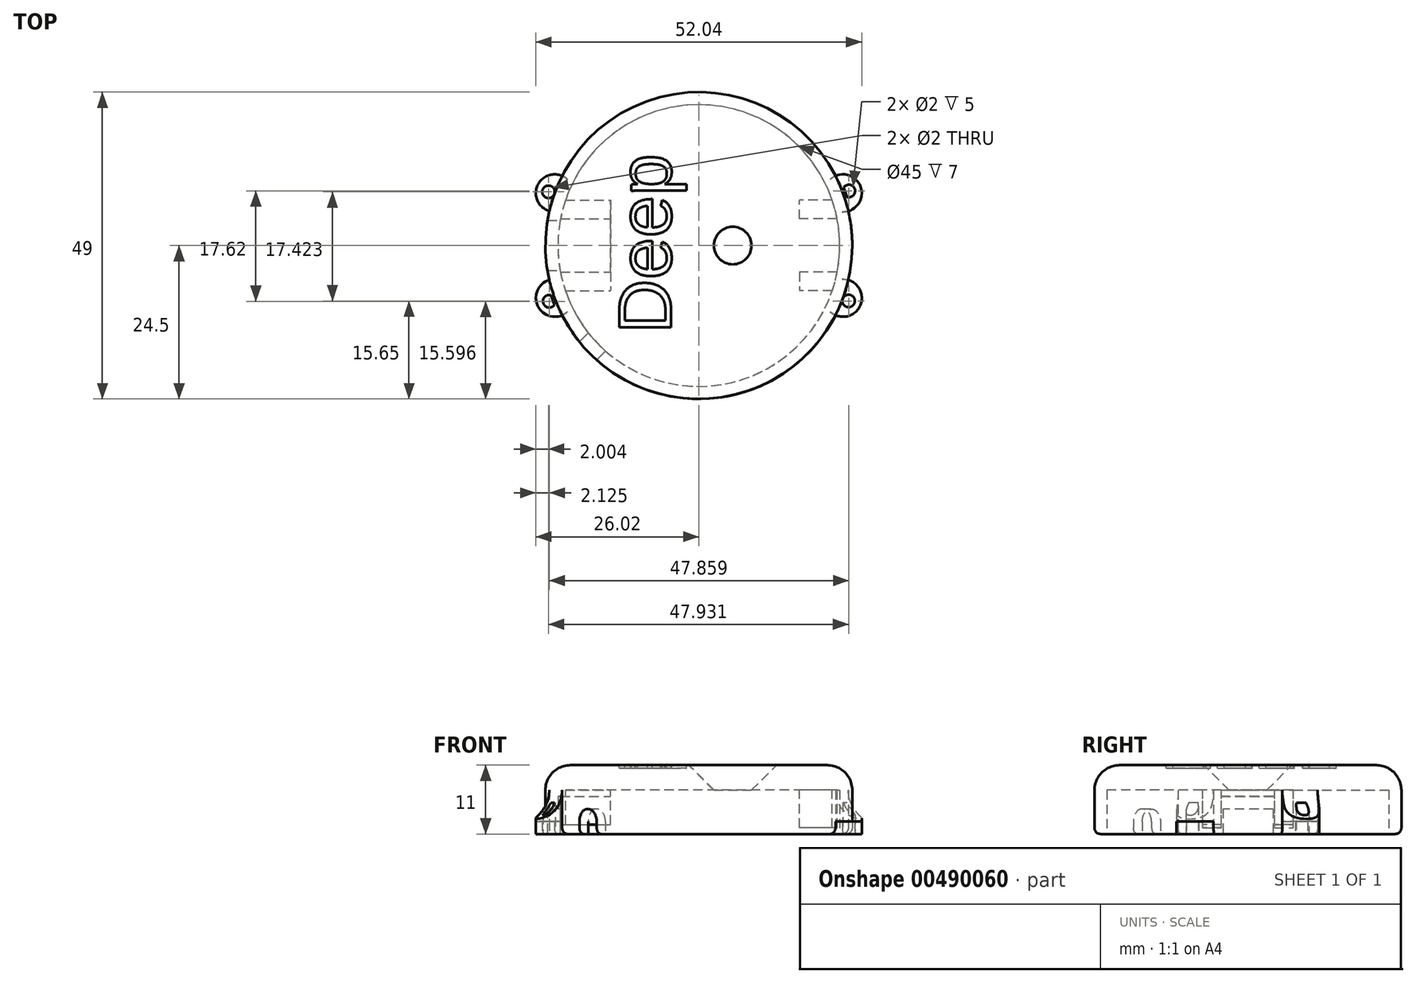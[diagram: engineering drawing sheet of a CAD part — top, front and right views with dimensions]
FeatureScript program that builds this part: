
annotation { "Feature Type Name" : "Feature", "Feature Type Description" : "" }
export const myFeature = defineFeature(function(context is Context, id is Id, definition is map)
    precondition{}
    {
        {
            var Q0;
            Q0=qCreatedBy(makeId("Top.planeOp"),FACE);
            var sketch = newSketch(context, id + "F0", { "sketchPlane" : qUnion([Q0])});
            skCircle(sketch, "E0", {"center": v(0, 0) * mm, "radius": 24.5 * mm});
            skSolve(sketch);
        }
        {
            var Q0;
            Q0=makeQuery(id+"F0.imprint","IMPRINT",FACE,{"disambiguationData":[TD([[makeQuery(id+"F0.imprint","IMPRINT",EDGE,{"derivedFrom":sQuery(id+"F0.wireOp",EDGE,"E0")}),1.0]])]});
            extrude(context, id + "F1", {"entities" : qUnion([Q0]), "depth" : 9 * mm});
        }
        {
            var Q0;
            Q0=makeQuery(id+"F1.opExtrude","CAP_FACE",FACE,{"disambiguationData":[OSD([sQuery(id+"F0.wireOp",EDGE,"E0")])],"isStart":true});
            shell(context, id + "F2", {"entities" : qUnion([Q0]), "thickness" : 2 * mm});
        }
        {
            var Q0;
            Q0=makeQuery(id+"F1.opExtrude","CAP_FACE",FACE,{"disambiguationData":[OSD([sQuery(id+"F0.wireOp",EDGE,"E0")])],"isStart":true});
            var sketch = newSketch(context, id + "F3", { "sketchPlane" : qUnion([Q0])});
            skLineSegment(sketch, "E1.bottom", {"start": v(-26.55, 4) * mm, "end": v(-19.55, 4) * mm});
            skLineSegment(sketch, "E1.top", {"start": v(-26.55, -4) * mm, "end": v(-19.55, -4) * mm});
            skLineSegment(sketch, "E1.left", {"start": v(-26.55, 4) * mm, "end": v(-26.55, -4) * mm});
            skLineSegment(sketch, "E1.right", {"start": v(-19.55, 4) * mm, "end": v(-19.55, -4) * mm});
            skSolve(sketch);
        }
        {
            var Q0;
            {var subQ0=sQuery(id+"F3.wireOp",EDGE,"E1.bottom");var subQ1=sQuery(id+"F0.wireOp",EDGE,"E0");var subQ2=makeQuery(id+"F1.opExtrude","CAP_EDGE",EDGE,{"disambiguationData":[OSD([subQ1])],"isStart":true});var subQ3=makeQuery(id+"F3.imprint","INTERSECT",VERTEX,{"derivedFrom":[subQ2,subQ0]});Q0=makeQuery(id+"F3.imprint","IMPRINT",FACE,{"disambiguationData":[TD([[makeQuery(id+"F3.imprint","IMPRINT",EDGE,{"disambiguationData":[TD([[subQ3,1.0]])],"derivedFrom":subQ2}),-1.0]])]});}
            extrude(context, id + "F4", {"entities" : qUnion([Q0]), "operationType" : NewBodyOperationType.REMOVE, "oppositeDirection" : true, "depth" : 5 * mm});
        }
        {
            var Q0;
            {var subQ0=sQuery(id+"F0.wireOp",EDGE,"E0");Q0=makeQuery(id+"F2.opShell","OFFSET_FACE",FACE,{"disambiguationData":[OSD([subQ0]),TDD([makeQuery(id+"F1.opExtrude","CAP_FACE",FACE,{"disambiguationData":[OSD([subQ0])],"isStart":false})])]});}
            var sketch = newSketch(context, id + "F5", { "sketchPlane" : qUnion([Q0])});
            skLineSegment(sketch, "E2.bottom", {"start": v(-22.1, 4.25) * mm, "end": v(-14.1, 4.25) * mm});
            skLineSegment(sketch, "E2.top", {"start": v(-22.1, 7.25) * mm, "end": v(-14.1, 7.25) * mm});
            skLineSegment(sketch, "E2.left", {"start": v(-22.1, 4.25) * mm, "end": v(-22.1, 7.25) * mm});
            skLineSegment(sketch, "E2.right", {"start": v(-14.1, 4.25) * mm, "end": v(-14.1, 7.25) * mm});
            skLineSegment(sketch, "E3.bottom", {"start": v(-22.1, -4.25) * mm, "end": v(-14.1, -4.25) * mm});
            skLineSegment(sketch, "E3.top", {"start": v(-22.1, -7.25) * mm, "end": v(-14.1, -7.25) * mm});
            skLineSegment(sketch, "E3.left", {"start": v(-22.1, -4.25) * mm, "end": v(-22.1, -7.25) * mm});
            skLineSegment(sketch, "E3.right", {"start": v(-14.1, -4.25) * mm, "end": v(-14.1, -7.25) * mm});
            skLineSegment(sketch, "E4.bottom", {"start": v(22.1, 4.25) * mm, "end": v(16.1, 4.25) * mm});
            skLineSegment(sketch, "E4.top", {"start": v(22.1, 7.25) * mm, "end": v(16.1, 7.25) * mm});
            skLineSegment(sketch, "E4.left", {"start": v(22.1, 4.25) * mm, "end": v(22.1, 7.25) * mm});
            skLineSegment(sketch, "E4.right", {"start": v(16.1, 4.25) * mm, "end": v(16.1, 7.25) * mm});
            skLineSegment(sketch, "E5.bottom", {"start": v(22.1, -4.25) * mm, "end": v(16.1, -4.25) * mm});
            skLineSegment(sketch, "E5.top", {"start": v(22.1, -7.25) * mm, "end": v(16.1, -7.25) * mm});
            skLineSegment(sketch, "E5.left", {"start": v(22.1, -4.25) * mm, "end": v(22.1, -7.25) * mm});
            skLineSegment(sketch, "E5.right", {"start": v(16.1, -4.25) * mm, "end": v(16.1, -7.25) * mm});
            skSolve(sketch);
        }
        {
            var Q0;
            {var subQ0=sQuery(id+"F5.wireOp",EDGE,"E2.bottom");Q0=makeQuery(id+"F5.imprint","IMPRINT",FACE,{"disambiguationData":[TD([[makeQuery(id+"F5.imprint","IMPRINT",EDGE,{"derivedFrom":subQ0}),1.0]])]});}
            var Q1;
            {var subQ0=sQuery(id+"F5.wireOp",EDGE,"E3.bottom");Q1=makeQuery(id+"F5.imprint","IMPRINT",FACE,{"disambiguationData":[TD([[makeQuery(id+"F5.imprint","IMPRINT",EDGE,{"derivedFrom":subQ0}),-1.0]])]});}
            var Q2;
            {var subQ0=sQuery(id+"F5.wireOp",EDGE,"E4.bottom");Q2=makeQuery(id+"F5.imprint","IMPRINT",FACE,{"disambiguationData":[TD([[makeQuery(id+"F5.imprint","IMPRINT",EDGE,{"derivedFrom":subQ0}),-1.0]])]});}
            var Q3;
            {var subQ0=sQuery(id+"F5.wireOp",EDGE,"E5.bottom");Q3=makeQuery(id+"F5.imprint","IMPRINT",FACE,{"disambiguationData":[TD([[makeQuery(id+"F5.imprint","IMPRINT",EDGE,{"derivedFrom":subQ0}),1.0]])]});}
            extrude(context, id + "F6", {"entities" : qUnion([Q0, Q1, Q2, Q3]), "operationType" : NewBodyOperationType.ADD, "depth" : 6 * mm});
        }
        {
            var Q0;
            Q0=makeQuery(id+"F1.opExtrude","CAP_FACE",FACE,{"disambiguationData":[OSD([sQuery(id+"F0.wireOp",EDGE,"E0")])],"isStart":true});
            var sketch = newSketch(context, id + "F7", { "sketchPlane" : qUnion([Q0])});
            skLineSegment(sketch, "E6", {"start": v(0, 0) * mm, "end": v(60.5, -22.02) * mm, "construction": true});
            skLineSegment(sketch, "E7", {"start": v(0, 0) * mm, "end": v(-61.16, 22.26) * mm, "construction": true});
            skLineSegment(sketch, "E8", {"start": v(0, 0) * mm, "end": v(57.48, 20.92) * mm, "construction": true});
            skLineSegment(sketch, "E9", {"start": v(0, 0) * mm, "end": v(-59.66, -21.71) * mm, "construction": true});
            skArc(sketch, "E10", {"start": v(-21.83, 11.13) * mm, "mid": v(-25.84, 9.4) * mm, "end": v(-23.87, 5.5) * mm});
            skPoint(sketch, "E10.startSnap0", {"position": v(-30.58, 11.13) * mm});
            skArc(sketch, "E11", {"start": v(-23.87, -5.5) * mm, "mid": v(-25.84, -9.4) * mm, "end": v(-21.83, -11.13) * mm});
            skArc(sketch, "E12", {"start": v(21.83, -11.13) * mm, "mid": v(25.84, -9.4) * mm, "end": v(23.87, -5.5) * mm});
            skArc(sketch, "E13", {"start": v(23.87, 5.5) * mm, "mid": v(25.84, 9.4) * mm, "end": v(21.83, 11.13) * mm});
            skSolve(sketch);
        }
        {
            var Q0;
            {var subQ0=sQuery(id+"F7.wireOp",EDGE,"E10");Q0=makeQuery(id+"F7.imprint","IMPRINT",FACE,{"disambiguationData":[TD([[makeQuery(id+"F7.imprint","IMPRINT",EDGE,{"derivedFrom":subQ0}),1.0]])]});}
            var Q1;
            {var subQ0=sQuery(id+"F7.wireOp",EDGE,"E13");Q1=makeQuery(id+"F7.imprint","IMPRINT",FACE,{"disambiguationData":[TD([[makeQuery(id+"F7.imprint","IMPRINT",EDGE,{"derivedFrom":subQ0}),1.0]])]});}
            var Q2;
            {var subQ0=sQuery(id+"F7.wireOp",EDGE,"E12");Q2=makeQuery(id+"F7.imprint","IMPRINT",FACE,{"disambiguationData":[TD([[makeQuery(id+"F7.imprint","IMPRINT",EDGE,{"derivedFrom":subQ0}),1.0]])]});}
            var Q3;
            {var subQ0=sQuery(id+"F7.wireOp",EDGE,"E11");Q3=makeQuery(id+"F7.imprint","IMPRINT",FACE,{"disambiguationData":[TD([[makeQuery(id+"F7.imprint","IMPRINT",EDGE,{"derivedFrom":subQ0}),1.0]])]});}
            var Q4;
            Q4=makeQuery(id+"F1.opExtrude","CAP_FACE",FACE,{"disambiguationData":[OSD([sQuery(id+"F0.wireOp",EDGE,"E0")])],"isStart":false});
            extrude(context, id + "F8", {"entities" : qUnion([Q0, Q1, Q2, Q3, Q4]), "operationType" : NewBodyOperationType.ADD, "oppositeDirection" : true, "depth" : 2 * mm});
        }
        {
            var Q0;
            {var subQ0=sQuery(id+"F7.wireOp",EDGE,"E11");var subQ1=sQuery(id+"F0.wireOp",EDGE,"E0");var subQ2=makeQuery(id+"F1.opExtrude","CAP_EDGE",EDGE,{"disambiguationData":[OSD([subQ1])],"isStart":true});Q0=makeQuery(id+"F8.opExtrude","CAP_EDGE",EDGE,{"disambiguationData":[OSD([subQ1]),TDD([makeQuery(id+"F7.imprint","IMPRINT",EDGE,{"disambiguationData":[TD([[makeQuery(id+"F7.imprint","INTERSECT",VERTEX,{"disambiguationData":[OD(0.0)],"derivedFrom":[subQ2,subQ0]}),1.0]])],"derivedFrom":subQ2})])],"isStart":false});}
            var Q1;
            {var subQ0=sQuery(id+"F7.wireOp",EDGE,"E10");var subQ1=sQuery(id+"F0.wireOp",EDGE,"E0");var subQ2=makeQuery(id+"F1.opExtrude","CAP_EDGE",EDGE,{"disambiguationData":[OSD([subQ1])],"isStart":true});Q1=makeQuery(id+"F8.opExtrude","CAP_EDGE",EDGE,{"disambiguationData":[OSD([subQ1]),TDD([makeQuery(id+"F7.imprint","IMPRINT",EDGE,{"disambiguationData":[TD([[makeQuery(id+"F7.imprint","INTERSECT",VERTEX,{"disambiguationData":[OD(0.0)],"derivedFrom":[subQ2,subQ0]}),1.0]])],"derivedFrom":subQ2})])],"isStart":false});}
            var Q2;
            {var subQ0=sQuery(id+"F7.wireOp",EDGE,"E12");var subQ1=sQuery(id+"F0.wireOp",EDGE,"E0");var subQ2=makeQuery(id+"F1.opExtrude","CAP_EDGE",EDGE,{"disambiguationData":[OSD([subQ1])],"isStart":true});Q2=makeQuery(id+"F8.opExtrude","CAP_EDGE",EDGE,{"disambiguationData":[OSD([subQ1]),TDD([makeQuery(id+"F7.imprint","IMPRINT",EDGE,{"disambiguationData":[TD([[makeQuery(id+"F7.imprint","INTERSECT",VERTEX,{"disambiguationData":[OD(0.0)],"derivedFrom":[subQ2,subQ0]}),1.0]])],"derivedFrom":subQ2})])],"isStart":false});}
            var Q3;
            {var subQ0=sQuery(id+"F7.wireOp",EDGE,"E13");var subQ1=sQuery(id+"F0.wireOp",EDGE,"E0");var subQ2=makeQuery(id+"F1.opExtrude","CAP_EDGE",EDGE,{"disambiguationData":[OSD([subQ1])],"isStart":true});Q3=makeQuery(id+"F8.opExtrude","CAP_EDGE",EDGE,{"disambiguationData":[OSD([subQ1]),TDD([makeQuery(id+"F7.imprint","IMPRINT",EDGE,{"disambiguationData":[TD([[makeQuery(id+"F7.imprint","INTERSECT",VERTEX,{"disambiguationData":[OD(0.0)],"derivedFrom":[subQ2,subQ0]}),1.0]])],"derivedFrom":subQ2})])],"isStart":false});}
            fillet(context, id + "F9", {"entities" : qUnion([Q0, Q1, Q2, Q3]), "radius" : 5 * mm, "tangentPropagation" : true, "allowEdgeOverflow" : false});
        }
        {
            var Q0;
            {var subQ0=sQuery(id+"F0.wireOp",EDGE,"E0");Q0=makeQuery(id+"F8.boolean.opBoolean","MERGE",FACE,{"derivedFrom":[makeQuery(id+"F1.opExtrude","CAP_FACE",FACE,{"disambiguationData":[OSD([subQ0])],"isStart":true}),makeQuery(id+"F8.opExtrude","CAP_FACE",FACE,{"disambiguationData":[OSD([subQ0,sQuery(id+"F7.wireOp",EDGE,"E10")])],"isStart":true}),makeQuery(id+"F8.opExtrude","CAP_FACE",FACE,{"disambiguationData":[OSD([subQ0,sQuery(id+"F7.wireOp",EDGE,"E11")])],"isStart":true}),makeQuery(id+"F8.opExtrude","CAP_FACE",FACE,{"disambiguationData":[OSD([subQ0,sQuery(id+"F7.wireOp",EDGE,"E12")])],"isStart":true}),makeQuery(id+"F8.opExtrude","CAP_FACE",FACE,{"disambiguationData":[OSD([subQ0,sQuery(id+"F7.wireOp",EDGE,"E13")])],"isStart":true})]});}
            var sketch = newSketch(context, id + "F10", { "sketchPlane" : qUnion([Q0])});
            skCircle(sketch, "E14", {"center": v(0, 0) * mm, "radius": 25.5 * mm, "construction": true});
            skCircle(sketch, "E15", {"center": v(-23.9, 8.9) * mm, "radius": 1 * mm});
            skPoint(sketch, "E15.centerSnap0", {"position": v(-25.84, 9.4) * mm});
            skCircle(sketch, "E16", {"center": v(23.91, 8.85) * mm, "radius": 1 * mm});
            skCircle(sketch, "E17", {"center": v(23.96, -8.72) * mm, "radius": 1 * mm});
            skCircle(sketch, "E18", {"center": v(-24.02, -8.57) * mm, "radius": 1 * mm});
            skSolve(sketch);
        }
        {
            var Q0;
            Q0=makeQuery(id+"F10.imprint","IMPRINT",FACE,{"disambiguationData":[TD([[makeQuery(id+"F10.imprint","IMPRINT",EDGE,{"derivedFrom":sQuery(id+"F10.wireOp",EDGE,"E15")}),1.0]])]});
            var Q1;
            Q1=makeQuery(id+"F10.imprint","IMPRINT",FACE,{"disambiguationData":[TD([[makeQuery(id+"F10.imprint","IMPRINT",EDGE,{"derivedFrom":sQuery(id+"F10.wireOp",EDGE,"E18")}),1.0]])]});
            var Q2;
            Q2=makeQuery(id+"F10.imprint","IMPRINT",FACE,{"disambiguationData":[TD([[makeQuery(id+"F10.imprint","IMPRINT",EDGE,{"derivedFrom":sQuery(id+"F10.wireOp",EDGE,"E17")}),1.0]])]});
            var Q3;
            Q3=makeQuery(id+"F10.imprint","IMPRINT",FACE,{"disambiguationData":[TD([[makeQuery(id+"F10.imprint","IMPRINT",EDGE,{"derivedFrom":sQuery(id+"F10.wireOp",EDGE,"E16")}),1.0]])]});
            extrude(context, id + "F11", {"entities" : qUnion([Q0, Q1, Q2, Q3]), "operationType" : NewBodyOperationType.REMOVE, "oppositeDirection" : true, "depth" : 5 * mm});
        }
        {
            var Q0;
            {var subQ0=sQuery(id+"F0.wireOp",EDGE,"E0");Q0=makeQuery(id+"F8.opExtrude","CAP_EDGE",EDGE,{"disambiguationData":[OSD([subQ0]),TDD([makeQuery(id+"F1.opExtrude","CAP_EDGE",EDGE,{"disambiguationData":[OSD([subQ0])],"isStart":false})])],"isStart":false});}
            fillet(context, id + "F12", {"entities" : qUnion([Q0]), "radius" : 4 * mm, "tangentPropagation" : true, "allowEdgeOverflow" : false});
        }
        {
            var Q0;
            {var subQ0=sQuery(id+"F0.wireOp",EDGE,"E0");Q0=makeQuery(id+"F8.boolean.opBoolean","MERGE",FACE,{"derivedFrom":[makeQuery(id+"F1.opExtrude","CAP_FACE",FACE,{"disambiguationData":[OSD([subQ0])],"isStart":true}),makeQuery(id+"F8.opExtrude","CAP_FACE",FACE,{"disambiguationData":[OSD([subQ0,sQuery(id+"F7.wireOp",EDGE,"E10")])],"isStart":true}),makeQuery(id+"F8.opExtrude","CAP_FACE",FACE,{"disambiguationData":[OSD([subQ0,sQuery(id+"F7.wireOp",EDGE,"E11")])],"isStart":true}),makeQuery(id+"F8.opExtrude","CAP_FACE",FACE,{"disambiguationData":[OSD([subQ0,sQuery(id+"F7.wireOp",EDGE,"E12")])],"isStart":true}),makeQuery(id+"F8.opExtrude","CAP_FACE",FACE,{"disambiguationData":[OSD([subQ0,sQuery(id+"F7.wireOp",EDGE,"E13")])],"isStart":true})]});}
            var sketch = newSketch(context, id + "F13", { "sketchPlane" : qUnion([Q0])});
            skLineSegment(sketch, "E19", {"start": v(-19.79, 16.1) * mm, "end": v(-16.96, 18.93) * mm});
            skLineSegment(sketch, "E20", {"start": v(-16.96, 18.93) * mm, "end": v(-14.13, 16.1) * mm});
            skLineSegment(sketch, "E21", {"start": v(-14.13, 16.1) * mm, "end": v(-16.96, 13.27) * mm});
            skLineSegment(sketch, "E22", {"start": v(-16.96, 13.27) * mm, "end": v(-19.79, 16.1) * mm});
            skSolve(sketch);
        }
        {
            var Q0;
            {var subQ0=sQuery(id+"F13.wireOp",EDGE,"E20");var subQ2=sQuery(id+"F0.wireOp",EDGE,"E0");var subQ4=makeQuery(id+"F1.opExtrude","CAP_EDGE",EDGE,{"disambiguationData":[OSD([subQ2])],"isStart":true});var subQ7=makeQuery(id+"F2.opShell","OFFSET_EDGE",EDGE,{"disambiguationData":[OSD([subQ2]),TDD([subQ4])]});var subQ8=makeQuery(id+"F13.imprint","INTERSECT",VERTEX,{"derivedFrom":[subQ7,subQ0]});Q0=makeQuery(id+"F13.imprint","IMPRINT",FACE,{"disambiguationData":[TD([[makeQuery(id+"F13.imprint","IMPRINT",EDGE,{"disambiguationData":[TD([[subQ8,1.0]])],"derivedFrom":subQ7}),1.0]])]});}
            extrude(context, id + "F14", {"entities" : qUnion([Q0]), "operationType" : NewBodyOperationType.REMOVE, "oppositeDirection" : true, "depth" : 4 * mm});
        }
        {
            var Q0;
            Q0=makeQuery(id+"F14.boolean.opBoolean","COPY",EDGE,{"derivedFrom":makeQuery(id+"F14.opExtrude","CAP_EDGE",EDGE,{"disambiguationData":[OSD([sQuery(id+"F13.wireOp",EDGE,"E20")])],"isStart":false})});
            var Q1;
            Q1=makeQuery(id+"F14.boolean.opBoolean","COPY",EDGE,{"derivedFrom":makeQuery(id+"F14.opExtrude","CAP_EDGE",EDGE,{"disambiguationData":[OSD([sQuery(id+"F13.wireOp",EDGE,"E22")])],"isStart":false})});
            fillet(context, id + "F15", {"entities" : qUnion([Q0, Q1]), "radius" : 2 * mm, "tangentPropagation" : true, "allowEdgeOverflow" : false});
        }
        {
            var Q0;
            {var subQ0=sQuery(id+"F7.wireOp",EDGE,"E10");var subQ1=sQuery(id+"F0.wireOp",EDGE,"E0");var subQ2=makeQuery(id+"F8.opExtrude","CAP_FACE",FACE,{"disambiguationData":[OSD([subQ1,subQ0])],"isStart":true});var subQ3=makeQuery(id+"F1.opExtrude","CAP_FACE",FACE,{"disambiguationData":[OSD([subQ1])],"isStart":true});var subQ4=makeQuery(id+"F8.opExtrude","CAP_FACE",FACE,{"disambiguationData":[OSD([subQ1,sQuery(id+"F7.wireOp",EDGE,"E11")])],"isStart":true});var subQ5=makeQuery(id+"F1.opExtrude","SWEPT_FACE",FACE,{"disambiguationData":[OSD([subQ1])]});var subQ6=makeQuery(id+"F8.opExtrude","CAP_FACE",FACE,{"disambiguationData":[OSD([subQ1,sQuery(id+"F7.wireOp",EDGE,"E12")])],"isStart":true});var subQ7=sQuery(id+"F7.wireOp",EDGE,"E13");var subQ8=makeQuery(id+"F8.opExtrude","SWEPT_FACE",FACE,{"disambiguationData":[OSD([subQ7])]});var subQ9=makeQuery(id+"F8.opExtrude","CAP_FACE",FACE,{"disambiguationData":[OSD([subQ1,subQ7])],"isStart":true});Q0=makeQuery(id+"F14.boolean.opBoolean","SPLIT",EDGE,{"disambiguationData":[TD([subQ8])],"derivedFrom":makeQuery(id+"F8.boolean.opBoolean","SPLIT",EDGE,{"disambiguationData":[TD([subQ5,subQ3,makeQuery(id+"F8.opExtrude","SWEPT_FACE",FACE,{"disambiguationData":[OSD([subQ0])]}),subQ2,subQ4,subQ6,subQ8,subQ9])],"derivedFrom":makeQuery(id+"F1.opExtrude","CAP_EDGE",EDGE,{"disambiguationData":[OSD([subQ1])],"isStart":true})})});}
            var Q1;
            {var subQ0=sQuery(id+"F0.wireOp",EDGE,"E0");var subQ1=sQuery(id+"F7.wireOp",EDGE,"E12");var subQ2=sQuery(id+"F7.wireOp",EDGE,"E13");Q1=makeQuery(id+"F8.boolean.opBoolean","SPLIT",EDGE,{"disambiguationData":[TD([makeQuery(id+"F1.opExtrude","SWEPT_FACE",FACE,{"disambiguationData":[OSD([subQ0])]}),makeQuery(id+"F1.opExtrude","CAP_FACE",FACE,{"disambiguationData":[OSD([subQ0])],"isStart":true}),makeQuery(id+"F8.opExtrude","CAP_FACE",FACE,{"disambiguationData":[OSD([subQ0,sQuery(id+"F7.wireOp",EDGE,"E10")])],"isStart":true}),makeQuery(id+"F8.opExtrude","CAP_FACE",FACE,{"disambiguationData":[OSD([subQ0,sQuery(id+"F7.wireOp",EDGE,"E11")])],"isStart":true}),makeQuery(id+"F8.opExtrude","SWEPT_FACE",FACE,{"disambiguationData":[OSD([subQ1])]}),makeQuery(id+"F8.opExtrude","CAP_FACE",FACE,{"disambiguationData":[OSD([subQ0,subQ1])],"isStart":true}),makeQuery(id+"F8.opExtrude","SWEPT_FACE",FACE,{"disambiguationData":[OSD([subQ2])]}),makeQuery(id+"F8.opExtrude","CAP_FACE",FACE,{"disambiguationData":[OSD([subQ0,subQ2])],"isStart":true})])],"derivedFrom":makeQuery(id+"F1.opExtrude","CAP_EDGE",EDGE,{"disambiguationData":[OSD([subQ0])],"isStart":true})});}
            var Q2;
            {var subQ0=sQuery(id+"F7.wireOp",EDGE,"E11");var subQ1=sQuery(id+"F0.wireOp",EDGE,"E0");var subQ2=sQuery(id+"F7.wireOp",EDGE,"E12");Q2=makeQuery(id+"F8.boolean.opBoolean","SPLIT",EDGE,{"disambiguationData":[TD([makeQuery(id+"F1.opExtrude","SWEPT_FACE",FACE,{"disambiguationData":[OSD([subQ1])]}),makeQuery(id+"F1.opExtrude","CAP_FACE",FACE,{"disambiguationData":[OSD([subQ1])],"isStart":true}),makeQuery(id+"F8.opExtrude","CAP_FACE",FACE,{"disambiguationData":[OSD([subQ1,sQuery(id+"F7.wireOp",EDGE,"E10")])],"isStart":true}),makeQuery(id+"F8.opExtrude","SWEPT_FACE",FACE,{"disambiguationData":[OSD([subQ0])]}),makeQuery(id+"F8.opExtrude","CAP_FACE",FACE,{"disambiguationData":[OSD([subQ1,subQ0])],"isStart":true}),makeQuery(id+"F8.opExtrude","SWEPT_FACE",FACE,{"disambiguationData":[OSD([subQ2])]}),makeQuery(id+"F8.opExtrude","CAP_FACE",FACE,{"disambiguationData":[OSD([subQ1,subQ2])],"isStart":true}),makeQuery(id+"F8.opExtrude","CAP_FACE",FACE,{"disambiguationData":[OSD([subQ1,sQuery(id+"F7.wireOp",EDGE,"E13")])],"isStart":true})])],"derivedFrom":makeQuery(id+"F1.opExtrude","CAP_EDGE",EDGE,{"disambiguationData":[OSD([subQ1])],"isStart":true})});}
            var Q3;
            {var subQ0=sQuery(id+"F7.wireOp",EDGE,"E10");var subQ1=sQuery(id+"F0.wireOp",EDGE,"E0");var subQ2=makeQuery(id+"F8.opExtrude","CAP_FACE",FACE,{"disambiguationData":[OSD([subQ1,subQ0])],"isStart":true});var subQ3=makeQuery(id+"F8.opExtrude","SWEPT_FACE",FACE,{"disambiguationData":[OSD([subQ0])]});var subQ4=makeQuery(id+"F1.opExtrude","CAP_FACE",FACE,{"disambiguationData":[OSD([subQ1])],"isStart":true});var subQ5=makeQuery(id+"F1.opExtrude","SWEPT_FACE",FACE,{"disambiguationData":[OSD([subQ1])]});var subQ6=makeQuery(id+"F8.opExtrude","CAP_FACE",FACE,{"disambiguationData":[OSD([subQ1,sQuery(id+"F7.wireOp",EDGE,"E11")])],"isStart":true});var subQ7=makeQuery(id+"F8.opExtrude","CAP_FACE",FACE,{"disambiguationData":[OSD([subQ1,sQuery(id+"F7.wireOp",EDGE,"E12")])],"isStart":true});var subQ8=sQuery(id+"F7.wireOp",EDGE,"E13");var subQ9=makeQuery(id+"F8.opExtrude","CAP_FACE",FACE,{"disambiguationData":[OSD([subQ1,subQ8])],"isStart":true});Q3=makeQuery(id+"F14.boolean.opBoolean","SPLIT",EDGE,{"disambiguationData":[TD([subQ3])],"derivedFrom":makeQuery(id+"F8.boolean.opBoolean","SPLIT",EDGE,{"disambiguationData":[TD([subQ5,subQ4,subQ3,subQ2,subQ6,subQ7,makeQuery(id+"F8.opExtrude","SWEPT_FACE",FACE,{"disambiguationData":[OSD([subQ8])]}),subQ9])],"derivedFrom":makeQuery(id+"F1.opExtrude","CAP_EDGE",EDGE,{"disambiguationData":[OSD([subQ1])],"isStart":true})})});}
            fillet(context, id + "F16", {"entities" : qUnion([Q0, Q1, Q2, Q3]), "radius" : 1 * mm, "tangentPropagation" : true, "allowEdgeOverflow" : false});
        }
        {
            var Q0;
            {var subQ0=sQuery(id+"F0.wireOp",EDGE,"E0");Q0=makeQuery(id+"F2.opShell","OFFSET_FACE",FACE,{"disambiguationData":[OSD([subQ0]),TDD([makeQuery(id+"F1.opExtrude","CAP_FACE",FACE,{"disambiguationData":[OSD([subQ0])],"isStart":false})])]});}
            var sketch = newSketch(context, id + "F17", { "sketchPlane" : qUnion([Q0])});
            skLineSegment(sketch, "E23.bottom", {"start": v(-22.1, 4.25) * mm, "end": v(-14.1, 4.25) * mm});
            skLineSegment(sketch, "E23.top", {"start": v(-22.1, -4.25) * mm, "end": v(-14.1, -4.25) * mm});
            skLineSegment(sketch, "E23.left", {"start": v(-22.1, 4.25) * mm, "end": v(-22.1, -4.25) * mm});
            skLineSegment(sketch, "E23.right", {"start": v(-14.1, 4.25) * mm, "end": v(-14.1, -4.25) * mm});
            skSolve(sketch);
        }
        {
            var Q0;
            Q0=makeQuery(id+"F17.imprint","IMPRINT",FACE,{"disambiguationData":[TD([[makeQuery(id+"F17.imprint","IMPRINT",EDGE,{"derivedFrom":sQuery(id+"F17.wireOp",EDGE,"E23.bottom")}),-1.0]])]});
            var Q1;
            Q1=makeQuery(id+"F17.imprint","IMPRINT",FACE,{"disambiguationData":[TD([[makeQuery(id+"F17.imprint","IMPRINT",EDGE,{"derivedFrom":sQuery(id+"F17.wireOp",EDGE,"E23.left")}),-1.0]])]});
            extrude(context, id + "F18", {"entities" : qUnion([Q0, Q1]), "operationType" : NewBodyOperationType.ADD, "depth" : 1 * mm, "offsetDistance" : 25 * mm});
        }
        {
            var Q0;
            Q0=makeQuery(id+"F8.opExtrude","CAP_FACE",FACE,{"disambiguationData":[OSD([sQuery(id+"F0.wireOp",EDGE,"E0")])],"isStart":false});
            var sketch = newSketch(context, id + "F19", { "sketchPlane" : qUnion([Q0])});
            skText(sketch, "E24", { "text": "Deep", "fontName": "Arimo-Regular.ttf"});
            skLineSegment(sketch, "E25", {"start": v(-33.44, 0) * mm, "end": v(36.86, 0) * mm, "construction": true});
            skLineSegment(sketch, "E26", {"start": v(0, 29.52) * mm, "end": v(0, -23) * mm, "construction": true});
            const initialGuessF19  = {"E24": [-0.00445, -0.01406, 0, 1, 0.00864]};
            skSetInitialGuess(sketch, initialGuessF19);
            skSolve(sketch);
        }
        {
            var Q0;
            Q0 = qSketchRegion(id + "F19", true);
            extrude(context, id + "F20", {"entities" : qUnion([Q0]), "operationType" : NewBodyOperationType.REMOVE, "oppositeDirection" : true, "depth" : .5 * mm, "offsetDistance" : 25 * mm});
        }
        {
            var Q0;
            {var subQ0=sQuery(id+"F0.wireOp",EDGE,"E0");Q0=makeQuery(id+"F2.opShell","OFFSET_FACE",FACE,{"disambiguationData":[OSD([subQ0]),TDD([makeQuery(id+"F1.opExtrude","CAP_FACE",FACE,{"disambiguationData":[OSD([subQ0])],"isStart":false})])]});}
            var sketch = newSketch(context, id + "F21", { "sketchPlane" : qUnion([Q0])});
            skCircle(sketch, "E27", {"center": v(5.4, 0) * mm, "radius": 3 * mm});
            skSolve(sketch);
        }
        {
            var Q0;
            Q0=makeQuery(id+"F21.imprint","IMPRINT",FACE,{"disambiguationData":[TD([[makeQuery(id+"F21.imprint","IMPRINT",EDGE,{"derivedFrom":sQuery(id+"F21.wireOp",EDGE,"E27")}),1.0]])]});
            extrude(context, id + "F22", {"entities" : qUnion([Q0]), "operationType" : NewBodyOperationType.REMOVE, "endBound" : BoundingType.THROUGH_ALL, "oppositeDirection" : true, "depth" : 25 * mm, "offsetDistance" : 25 * mm});
        }
        {
            var Q0;
            Q0=makeQuery(id+"F22.boolean.opBoolean","INTERSECT",EDGE,{"derivedFrom":[makeQuery(id+"F8.opExtrude","CAP_FACE",FACE,{"disambiguationData":[OSD([sQuery(id+"F0.wireOp",EDGE,"E0")])],"isStart":false}),makeQuery(id+"F22.opExtrude","SWEPT_FACE",FACE,{"disambiguationData":[OSD([sQuery(id+"F21.wireOp",EDGE,"E27")])]})]});
            chamfer(context, id + "F23", {"entities" : qUnion([Q0]), "width" : 4 * mm, "tangentPropagation" : true});
        }
        {
            var Q0;
            {var subQ0=makeQuery(id+"F8.opExtrude","CAP_FACE",FACE,{"disambiguationData":[OSD([sQuery(id+"F0.wireOp",EDGE,"E0")])],"isStart":false});Q0=makeQuery(id+"F23.opChamfer","BLEND_EDGE",EDGE,{"blendedFrom":[makeQuery(id+"F22.boolean.opBoolean","INTERSECT",EDGE,{"derivedFrom":[subQ0,makeQuery(id+"F22.opExtrude","SWEPT_FACE",FACE,{"disambiguationData":[OSD([sQuery(id+"F21.wireOp",EDGE,"E27")])]})]}),subQ0],"blendedInto":[subQ0]});}
            fillet(context, id + "F24", {"entities" : qUnion([Q0]), "radius" : 1 * mm, "tangentPropagation" : true, "allowEdgeOverflow" : false});
        }
        {
            var Q0;
            Q0=makeQuery(id+"F4.boolean.opBoolean","COPY",FACE,{"derivedFrom":makeQuery(id+"F4.opExtrude","CAP_FACE",FACE,{"disambiguationData":[OSD([sQuery(id+"F0.wireOp",EDGE,"E0"),sQuery(id+"F3.wireOp",EDGE,"E1.bottom"),sQuery(id+"F3.wireOp",EDGE,"E1.top")])],"isStart":false})});
            extrude(context, id + "F25", {"entities" : qUnion([Q0]), "operationType" : NewBodyOperationType.ADD, "depth" : 1 * mm, "offsetDistance" : 25 * mm});
        }
        {
            var Q0;
            Q0=makeQuery(id+"F6.opExtrude","CAP_FACE",FACE,{"disambiguationData":[OSD([sQuery(id+"F0.wireOp",EDGE,"E0"),sQuery(id+"F5.wireOp",EDGE,"E3.bottom"),sQuery(id+"F5.wireOp",EDGE,"E3.top"),sQuery(id+"F5.wireOp",EDGE,"E3.right")])],"isStart":false});
            var Q1;
            Q1=makeQuery(id+"F6.opExtrude","CAP_FACE",FACE,{"disambiguationData":[OSD([sQuery(id+"F0.wireOp",EDGE,"E0"),sQuery(id+"F5.wireOp",EDGE,"E2.bottom"),sQuery(id+"F5.wireOp",EDGE,"E2.top"),sQuery(id+"F5.wireOp",EDGE,"E2.right")])],"isStart":false});
            extrude(context, id + "F26", {"entities" : qUnion([Q0, Q1]), "operationType" : NewBodyOperationType.REMOVE, "oppositeDirection" : true, "depth" : .5 * mm, "offsetDistance" : 25 * mm});
        }
    });
